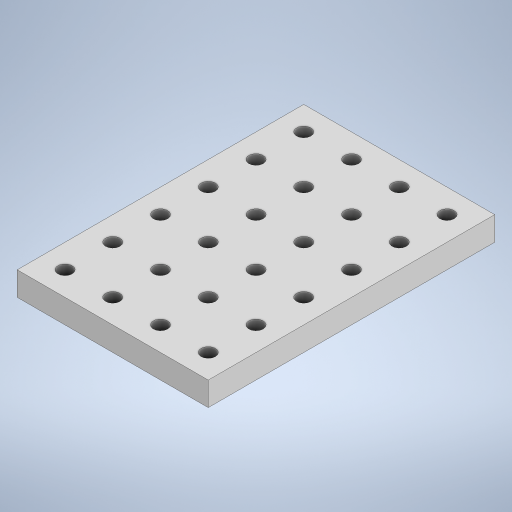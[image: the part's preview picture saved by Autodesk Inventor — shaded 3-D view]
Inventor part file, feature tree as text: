
AUTODESK INVENTOR PART (.ipt)
format: ipt  version: 2024 (Build 280153000, 153)  size: 249,856 bytes
history: native  units: in
note: dims shown in document units (in); Inventor stores cm internally (conversion verified against a paired STEP export)
features: extrude x2, sketch x2, pattern_linear x1
ambient origin geometry x8: Origin, YZ Plane, XZ Plane, XY Plane, X Axis, Y Axis, Z Axis, Center Point
bodies: Solid1 (feature_tree)
feature tree (5):
  extrude  "Extrusion1"  Depth=6.0in
  extrude  "Extrusion2"  Depth=0.5in
  pattern_linear  "Rectangular Pattern1"  Spacing1=0.5in  [1 undecoded]
  sketch  "Sketch1"  dims[d0=4.0in d1=6.0in]
  sketch  "Sketch2"  dims[d2=0.5in d3=0.0in d4=0.3in d5=0.5in d6=0.5in d7=0.5in d8=0.0in d9=2.3622in d11=1.0in d12=1.5748in d14=1.0in]
note: 1 required parameter value undecoded (feature->parameter linkage not recoverable at this tier; creation-order binding heuristic only, values carry confidence <= 0.55)
